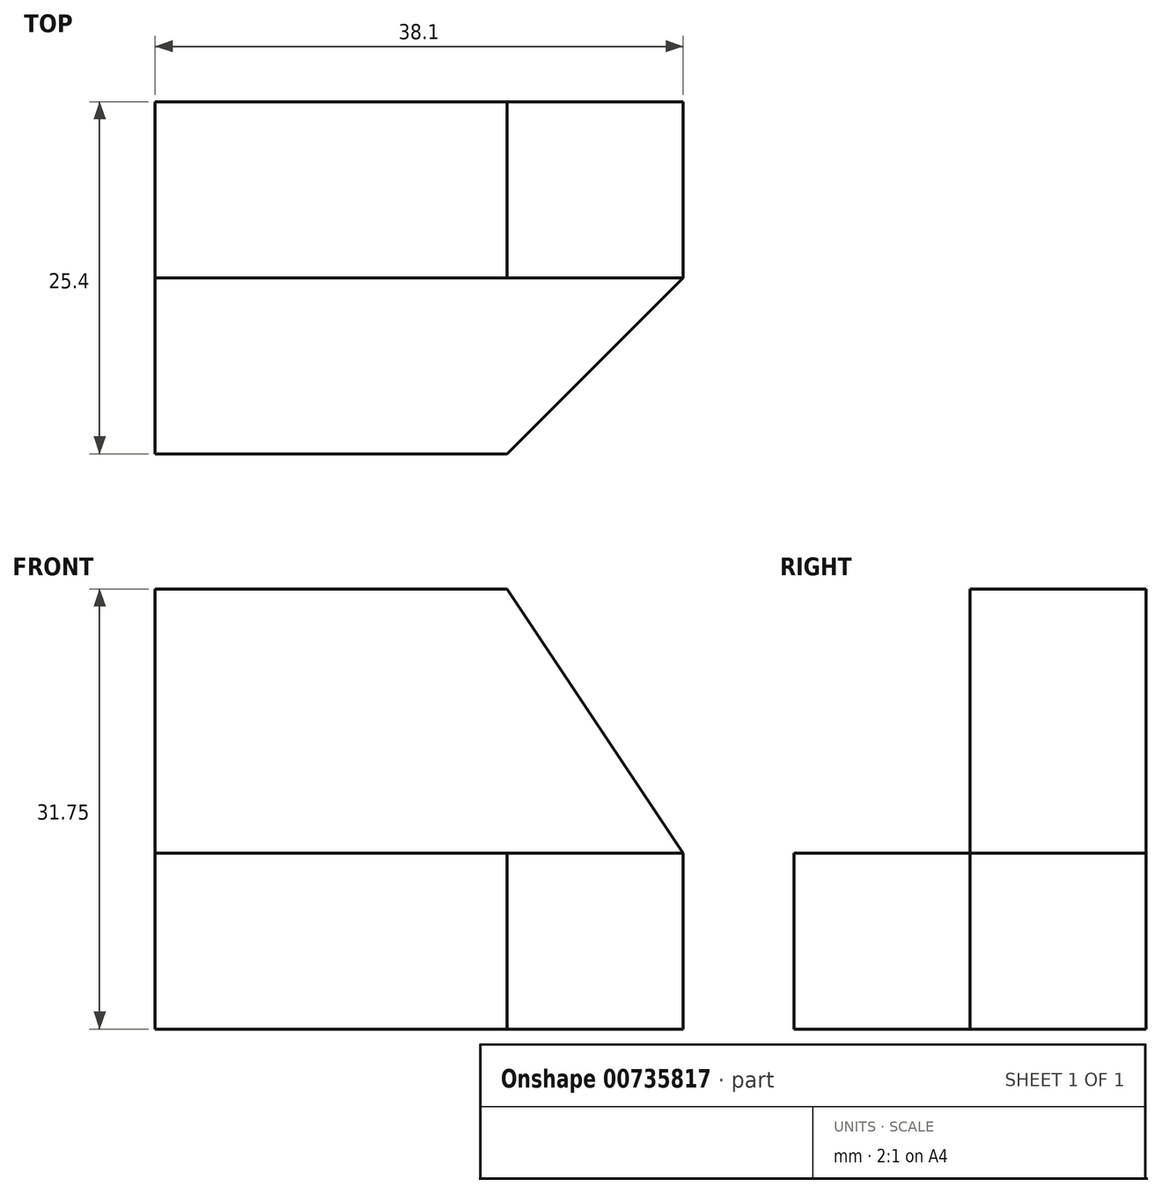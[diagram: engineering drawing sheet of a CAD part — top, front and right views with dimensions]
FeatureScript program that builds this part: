
annotation { "Feature Type Name" : "Feature", "Feature Type Description" : "" }
export const myFeature = defineFeature(function(context is Context, id is Id, definition is map)
    precondition{}
    {
        {
            var Q0;
            Q0=qCreatedBy(makeId("Front.planeOp"),FACE);
            var sketch = newSketch(context, id + "F0", { "sketchPlane" : qUnion([Q0])});
            skLineSegment(sketch, "E0", {"start": v(0, 0) * mm, "end": v(0, 31.75) * mm});
            skLineSegment(sketch, "E1", {"start": v(0, 31.75) * mm, "end": v(25.4, 31.75) * mm});
            skLineSegment(sketch, "E2", {"start": v(25.4, 31.75) * mm, "end": v(38.1, 12.7) * mm});
            skLineSegment(sketch, "E3", {"start": v(38.1, 12.7) * mm, "end": v(38.1, 0) * mm});
            skLineSegment(sketch, "E4", {"start": v(38.1, 0) * mm, "end": v(0, 0) * mm});
            skSolve(sketch);
        }
        {
            var Q0;
            Q0 = qSketchRegion(id + "F0", true);
            extrude(context, id + "F1", {"entities" : qUnion([Q0]), "depth" : 12.7 * mm, "offsetDistance" : 25.4 * mm});
        }
        {
            var Q0;
            Q0=makeQuery(id+"F1.opExtrude","CAP_FACE",FACE,{"disambiguationData":[OSD([sQuery(id+"F0.wireOp",EDGE,"E0"),sQuery(id+"F0.wireOp",EDGE,"E1"),sQuery(id+"F0.wireOp",EDGE,"E2"),sQuery(id+"F0.wireOp",EDGE,"E3"),sQuery(id+"F0.wireOp",EDGE,"E4")])],"isStart":false});
            var sketch = newSketch(context, id + "F2", { "sketchPlane" : qUnion([Q0])});
            skLineSegment(sketch, "E5", {"start": v(0, 12.7) * mm, "end": v(38.1, 12.7) * mm});
            skLineSegment(sketch, "E6", {"start": v(38.1, 12.7) * mm, "end": v(38.1, 0) * mm});
            skLineSegment(sketch, "E7", {"start": v(38.1, 0) * mm, "end": v(0, 0) * mm});
            skLineSegment(sketch, "E8", {"start": v(0, 0) * mm, "end": v(0, 12.7) * mm});
            skSolve(sketch);
        }
        {
            var Q0;
            Q0 = qSketchRegion(id + "F2", true);
            extrude(context, id + "F3", {"entities" : qUnion([Q0]), "operationType" : NewBodyOperationType.ADD, "depth" : 12.7 * mm, "offsetDistance" : 25.4 * mm});
        }
        {
            var Q0;
            Q0=makeQuery(id+"F3.opExtrude","SWEPT_FACE",FACE,{"disambiguationData":[OSD([sQuery(id+"F2.wireOp",EDGE,"E5")])]});
            var sketch = newSketch(context, id + "F4", { "sketchPlane" : qUnion([Q0])});
            skLineSegment(sketch, "E9", {"start": v(38.1, -12.7) * mm, "end": v(25.4, -25.4) * mm});
            skLineSegment(sketch, "E10", {"start": v(25.4, -25.4) * mm, "end": v(25.4, -38.1) * mm});
            skLineSegment(sketch, "E11", {"start": v(25.4, -38.1) * mm, "end": v(38.1, -38.1) * mm});
            skLineSegment(sketch, "E12", {"start": v(38.1, -38.1) * mm, "end": v(38.1, -25.4) * mm});
            skLineSegment(sketch, "E13", {"start": v(38.1, -25.4) * mm, "end": v(38.1, -12.7) * mm});
            skSolve(sketch);
        }
        {
            var Q0;
            Q0 = qSketchRegion(id + "F4", true);
            extrude(context, id + "F5", {"entities" : qUnion([Q0]), "operationType" : NewBodyOperationType.REMOVE, "oppositeDirection" : true, "depth" : 25.4 * mm, "offsetDistance" : 25.4 * mm});
        }
    });
